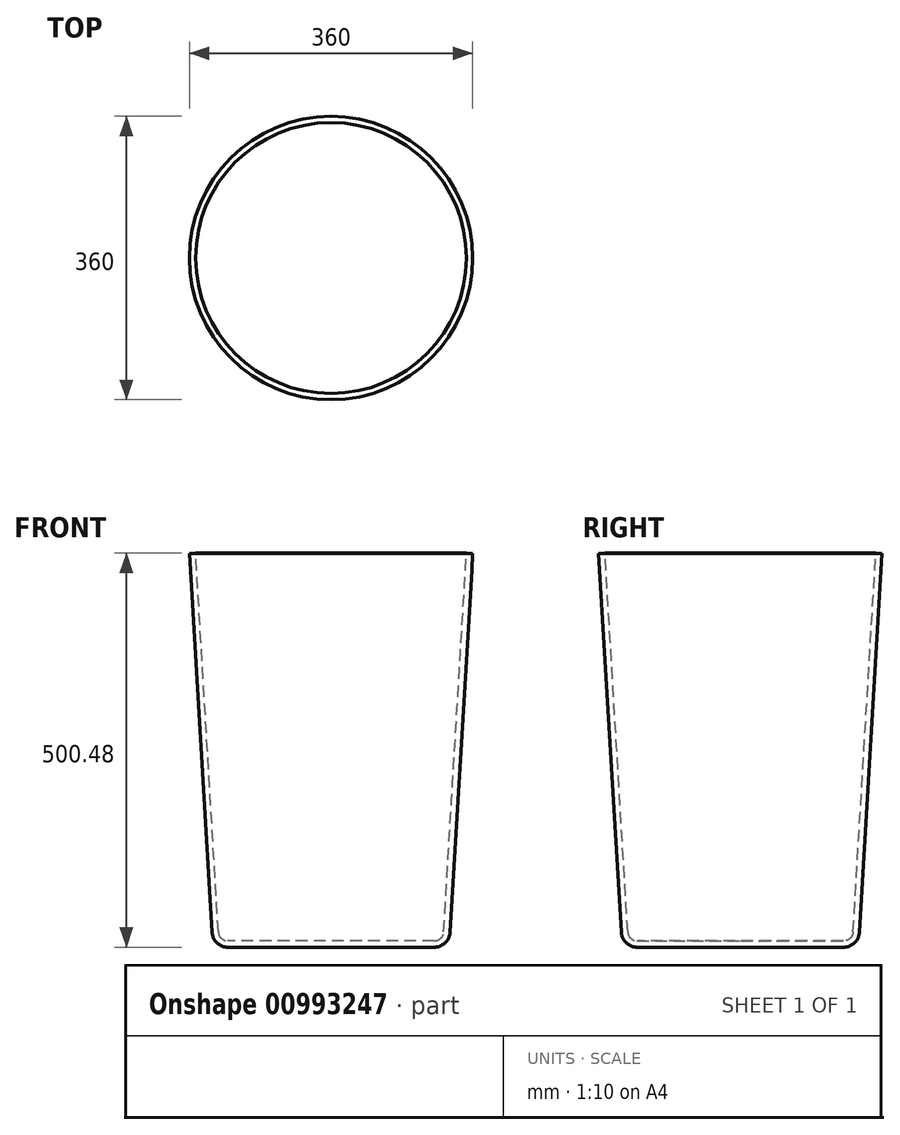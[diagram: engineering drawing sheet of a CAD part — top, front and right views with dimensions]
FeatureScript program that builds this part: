
annotation { "Feature Type Name" : "Feature", "Feature Type Description" : "" }
export const myFeature = defineFeature(function(context is Context, id is Id, definition is map)
    precondition{}
    {
        {
            var Q0;
            Q0=qCreatedBy(makeId("Front.planeOp"),FACE);
            var sketch = newSketch(context, id + "F0", { "sketchPlane" : qUnion([Q0])});
            skLineSegment(sketch, "E0", {"start": v(151.13, -181.2) * mm, "end": v(180, 300) * mm});
            skLineSegment(sketch, "E1", {"start": v(0, 218.46) * mm, "end": v(0, -227.7) * mm, "construction": true});
            skLineSegment(sketch, "E2", {"start": v(131.16, -200) * mm, "end": v(0, -200) * mm});
            skLineSegment(sketch, "E3", {"start": v(0, -200) * mm, "end": v(0, -206.1) * mm});
            skPoint(sketch, "E4.visualSharp", {"position": v(150, -200) * mm});
            skArc(sketch, "E4.filletArc", {"start": v(131.16, -200) * mm, "mid": v(144.88, -194.56) * mm, "end": v(151.13, -181.2) * mm});
            skLineSegment(sketch, "E5.filletArc", {"start": v(122.78, -208.1) * mm, "end": v(122.78, -208.1) * mm});
            skArc(sketch, "E6.0", {"start": v(131.16, -192) * mm, "mid": v(139.4, -188.74) * mm, "end": v(143.14, -180.72) * mm});
            skLineSegment(sketch, "E7.0", {"start": v(131.16, -192) * mm, "end": v(0, -192) * mm});
            skLineSegment(sketch, "E8.0", {"start": v(143.14, -180.72) * mm, "end": v(172.01, 300.48) * mm});
            skLineSegment(sketch, "E9", {"start": v(0, -200) * mm, "end": v(0, -192) * mm});
            skLineSegment(sketch, "E10", {"start": v(172.01, 300.48) * mm, "end": v(180, 300) * mm});
            skSolve(sketch);
        }
        {
            var Q0;
            Q0 = qSketchRegion(id + "F0", true);
            var Q1;
            Q1=sQuery(id+"F0.wireOp",EDGE,"E1");
            revolve(context, id + "F1", {"surfaceOperationType" : NewSurfaceOperationType.NEW, "entities" : qUnion([Q0]), "axis" : qUnion([Q1]), "revolveType" : RevolveType.FULL});
        }
    });
